# Revit family: 596_Alta Group_Станция глубокой биохимической очистки_Alta Air Master Pro 40
name_source: partatom
category: Оборудование
revit_build: Autodesk Revit 2017 (Build: 20171027_0315(x64)
units: mm (PartAtom-declared; Revit-internal decimal feet)

## family parameters
Всегда вертикально = Да
На основе рабочей плоскости = Нет
Общий = Нет
При загрузке вырезать с полостями = Нет
Размер круглого соединителя = Использовать диаметр
Тип детали = Нормальный
Точка расчета площади = Нет

## types (1)
- 596_Alta Group_Станция глубокой биохимической очистки_Alta Air Master Pro 40
    ADSK_URL страницы изделия = https://alta-group.ru
    ADSK_Версия Revit = Revit 2017
    ADSK_Единица измерения = шт.
    ADSK_Завод-изготовитель = Alta Group
    ADSK_Количество = 2
    ADSK_Марка = Alta Air Master Pro 40
    ADSK_Наименование = Станция глубокой биохимической очистки
    ADSK_Напряжение = 380 В
    ADSK_Номинальная мощность = 3710 Вт
    ADSK_Обозначение = Alta Air Master Pro 40
    ADSK_Размер_Высота = 3806 мм
    ADSK_Размер_Глубина = 2160 мм
    ADSK_Размер_Диаметр = 160 мм
    ADSK_Размер_Ширина = 9700 мм
    Глубина = 2000 мм
    Изготовитель = Alta Group
    Описание = Станция глубокой биохимической очистки
Производительность 40м3/сут, среднечасовое поступление стока 1.67 м3/час, 
Колличество вентмодулей 1шт,
Установочная мощность 3.71кВт/ч.
    Цвет корпуса = Зелёный
    Ширина_1 = 4540 мм
    Ширина_2 = 4540 мм
